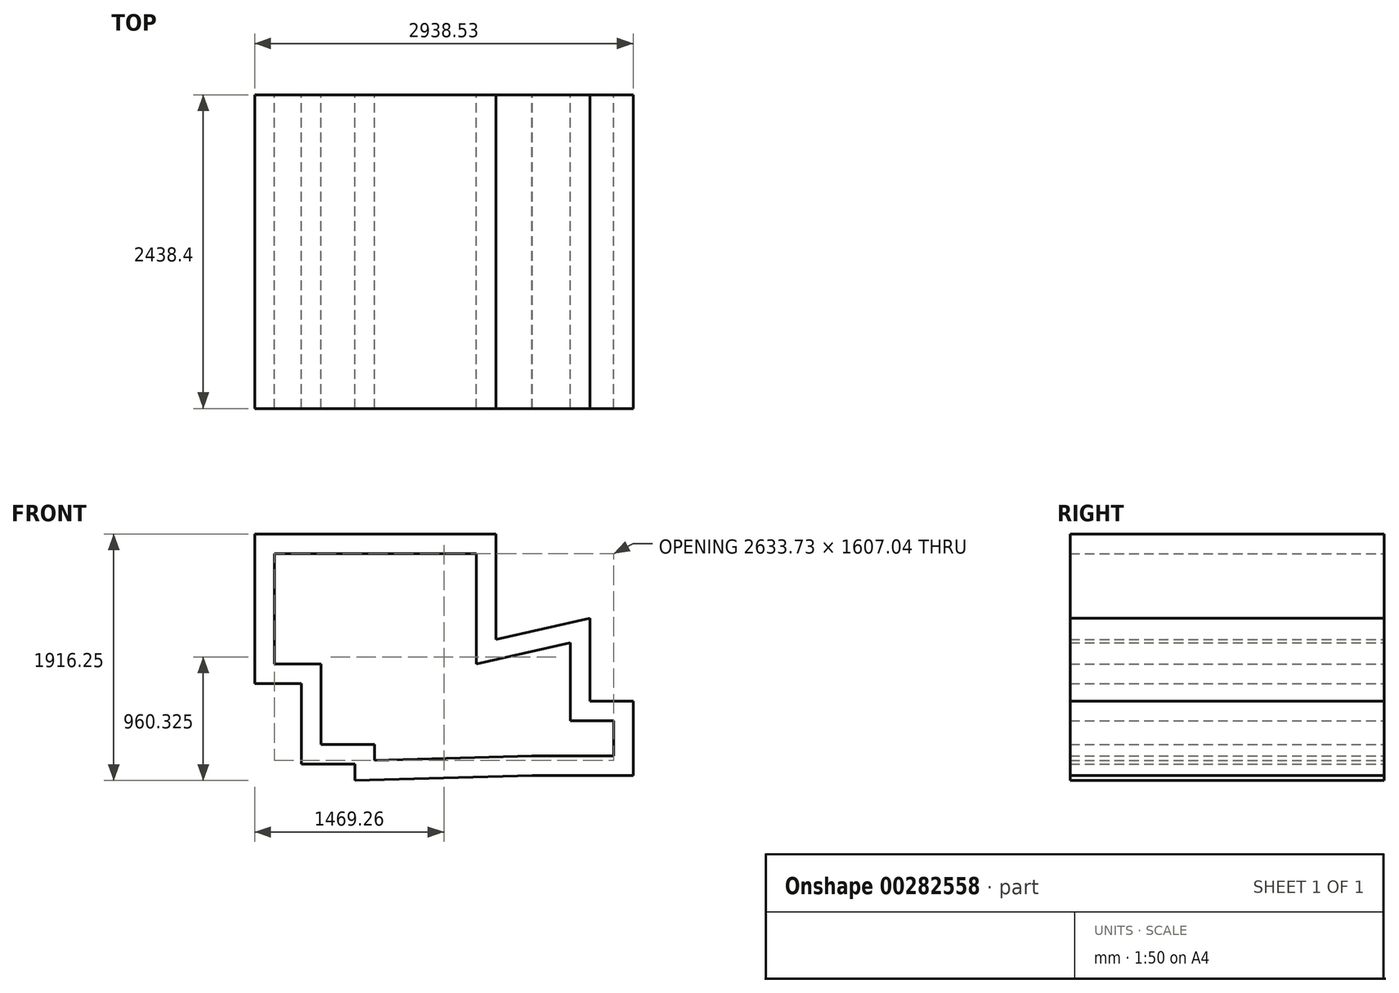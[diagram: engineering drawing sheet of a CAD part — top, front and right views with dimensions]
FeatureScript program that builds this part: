
annotation { "Feature Type Name" : "Feature", "Feature Type Description" : "" }
export const myFeature = defineFeature(function(context is Context, id is Id, definition is map)
    precondition{}
    {
        {
            var Q0;
            Q0=qCreatedBy(makeId("Front.planeOp"),FACE);
            var sketch = newSketch(context, id + "F0", { "sketchPlane" : qUnion([Q0])});
            skLineSegment(sketch, "E0", {"start": v(44.55, 367.86) * mm, "end": v(44.55, 491.87) * mm});
            skLineSegment(sketch, "E1", {"start": v(44.55, 491.87) * mm, "end": v(-372.53, 491.87) * mm});
            skLineSegment(sketch, "E2", {"start": v(-372.53, 491.87) * mm, "end": v(-372.53, 1116.83) * mm});
            skLineSegment(sketch, "E3", {"start": v(-372.53, 1116.83) * mm, "end": v(-734.61, 1116.83) * mm});
            skLineSegment(sketch, "E4", {"start": v(-734.61, 1116.83) * mm, "end": v(-734.61, 1974.9) * mm});
            skLineSegment(sketch, "E5", {"start": v(-734.61, 1974.9) * mm, "end": v(832.75, 1974.9) * mm});
            skLineSegment(sketch, "E6", {"start": v(832.75, 1116.83) * mm, "end": v(1563.9, 1282.69) * mm});
            skLineSegment(sketch, "E7", {"start": v(1563.9, 1282.69) * mm, "end": v(1563.9, 675.39) * mm});
            skLineSegment(sketch, "E8", {"start": v(1563.9, 675.39) * mm, "end": v(1899.12, 675.39) * mm});
            skLineSegment(sketch, "E9", {"start": v(1899.12, 675.39) * mm, "end": v(1899.12, 402.65) * mm});
            skLineSegment(sketch, "E10", {"start": v(1899.12, 402.65) * mm, "end": v(1266.97, 402.65) * mm});
            skLineSegment(sketch, "E11", {"start": v(1266.97, 402.65) * mm, "end": v(44.55, 367.86) * mm});
            skLineSegment(sketch, "E12", {"start": v(832.75, 1974.9) * mm, "end": v(832.75, 1116.83) * mm});
            skLineSegment(sketch, "E13.0", {"start": v(-887.01, 964.43) * mm, "end": v(-887.01, 2127.3) * mm});
            skLineSegment(sketch, "E13.1", {"start": v(-524.93, 964.43) * mm, "end": v(-887.01, 964.43) * mm});
            skLineSegment(sketch, "E13.2", {"start": v(1716.3, 827.79) * mm, "end": v(2051.52, 827.79) * mm});
            skLineSegment(sketch, "E13.3", {"start": v(1716.3, 1473.53) * mm, "end": v(1716.3, 827.79) * mm});
            skLineSegment(sketch, "E13.4", {"start": v(985.15, 1307.67) * mm, "end": v(1716.3, 1473.53) * mm});
            skLineSegment(sketch, "E13.5", {"start": v(985.15, 2127.3) * mm, "end": v(985.15, 1307.67) * mm});
            skLineSegment(sketch, "E13.6", {"start": v(2051.52, 827.79) * mm, "end": v(2051.52, 250.25) * mm});
            skLineSegment(sketch, "E13.7", {"start": v(2051.52, 250.25) * mm, "end": v(1269.14, 250.25) * mm});
            skLineSegment(sketch, "E13.8", {"start": v(-887.01, 2127.3) * mm, "end": v(985.15, 2127.3) * mm});
            skLineSegment(sketch, "E13.9", {"start": v(1269.14, 250.25) * mm, "end": v(-107.85, 211.06) * mm});
            skLineSegment(sketch, "E13.10", {"start": v(-107.85, 211.06) * mm, "end": v(-107.85, 339.47) * mm});
            skLineSegment(sketch, "E13.11", {"start": v(-107.85, 339.47) * mm, "end": v(-524.93, 339.47) * mm});
            skLineSegment(sketch, "E13.12", {"start": v(-524.93, 339.47) * mm, "end": v(-524.93, 964.43) * mm});
            skSolve(sketch);
        }
        {
            var Q0;
            Q0=makeQuery(id+"F0.imprint","IMPRINT",FACE,{"disambiguationData":[TD([[makeQuery(id+"F0.imprint","IMPRINT",EDGE,{"derivedFrom":sQuery(id+"F0.wireOp",EDGE,"E0")}),1.0]])]});
            extrude(context, id + "F1", {"entities" : qUnion([Q0]), "depth" : 2438.4 * mm});
        }
    });
